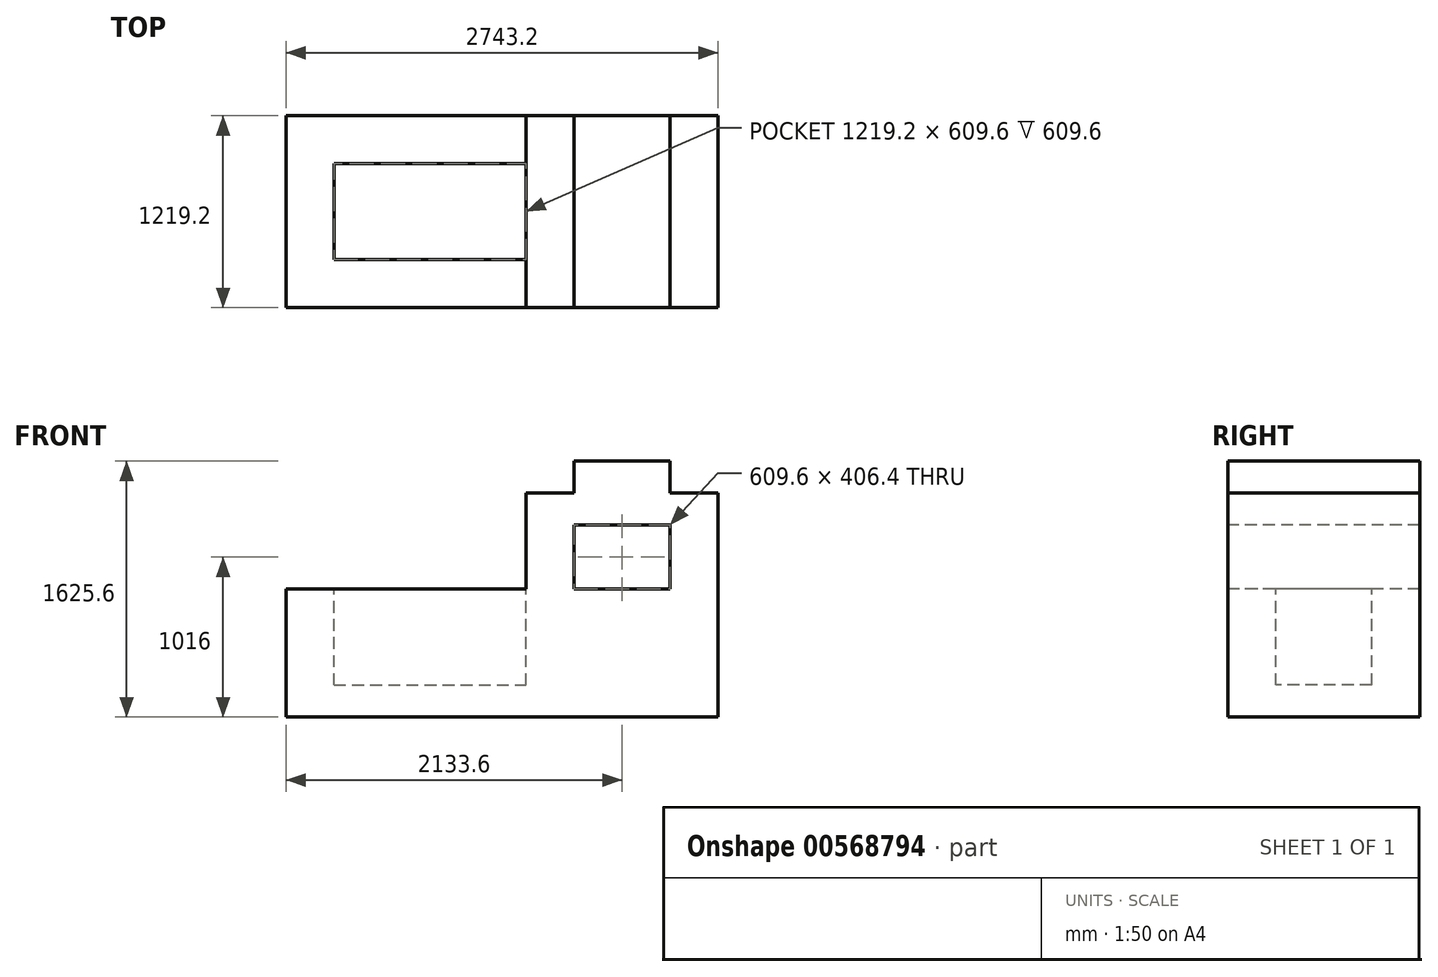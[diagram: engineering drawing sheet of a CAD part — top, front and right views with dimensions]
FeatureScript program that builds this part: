
annotation { "Feature Type Name" : "Feature", "Feature Type Description" : "" }
export const myFeature = defineFeature(function(context is Context, id is Id, definition is map)
    precondition{}
    {
        {
            var Q0;
            Q0=qCreatedBy(makeId("Front.planeOp"),FACE);
            var sketch = newSketch(context, id + "F0", { "sketchPlane" : qUnion([Q0])});
            skLineSegment(sketch, "E0.bottom", {"start": v(0, 0) * mm, "end": v(2743.2, 0) * mm});
            skLineSegment(sketch, "E0.top", {"start": v(0, 1625.6) * mm, "end": v(2743.2, 1625.6) * mm});
            skLineSegment(sketch, "E0.left", {"start": v(0, 0) * mm, "end": v(0, 1625.6) * mm});
            skLineSegment(sketch, "E0.right", {"start": v(2743.2, 0) * mm, "end": v(2743.2, 1625.6) * mm});
            skSolve(sketch);
        }
        {
            var Q0;
            Q0=makeQuery(id+"F0.imprint","IMPRINT",FACE,{"disambiguationData":[TD([[makeQuery(id+"F0.imprint","IMPRINT",EDGE,{"derivedFrom":sQuery(id+"F0.wireOp",EDGE,"E0.bottom")}),1.0]])]});
            extrude(context, id + "F1", {"entities" : qUnion([Q0]), "depth" : 1219.2 * mm, "offsetDistance" : 25.4 * mm});
        }
        {
            var Q0;
            Q0=makeQuery(id+"F1.opExtrude","CAP_FACE",FACE,{"disambiguationData":[OSD([sQuery(id+"F0.wireOp",EDGE,"E0.bottom"),sQuery(id+"F0.wireOp",EDGE,"E0.top"),sQuery(id+"F0.wireOp",EDGE,"E0.left"),sQuery(id+"F0.wireOp",EDGE,"E0.right")])],"isStart":false});
            var sketch = newSketch(context, id + "F2", { "sketchPlane" : qUnion([Q0])});
            skLineSegment(sketch, "E1.bottom", {"start": v(2743.2, 1625.6) * mm, "end": v(2438.4, 1625.6) * mm});
            skLineSegment(sketch, "E1.top", {"start": v(2743.2, 1422.4) * mm, "end": v(2438.4, 1422.4) * mm});
            skLineSegment(sketch, "E1.left", {"start": v(2743.2, 1625.6) * mm, "end": v(2743.2, 1422.4) * mm});
            skLineSegment(sketch, "E1.right", {"start": v(2438.4, 1625.6) * mm, "end": v(2438.4, 1422.4) * mm});
            skSolve(sketch);
        }
        {
            var Q0;
            Q0=makeQuery(id+"F2.imprint","IMPRINT",FACE,{"disambiguationData":[TD([[makeQuery(id+"F2.imprint","IMPRINT",EDGE,{"derivedFrom":sQuery(id+"F2.wireOp",EDGE,"E1.bottom")}),-1.0]])]});
            extrude(context, id + "F3", {"entities" : qUnion([Q0]), "operationType" : NewBodyOperationType.REMOVE, "endBound" : BoundingType.THROUGH_ALL, "oppositeDirection" : true, "depth" : 25.4 * mm, "offsetDistance" : 25.4 * mm});
        }
        {
            var Q0;
            Q0=makeQuery(id+"F1.opExtrude","CAP_FACE",FACE,{"disambiguationData":[OSD([sQuery(id+"F0.wireOp",EDGE,"E0.bottom"),sQuery(id+"F0.wireOp",EDGE,"E0.top"),sQuery(id+"F0.wireOp",EDGE,"E0.left"),sQuery(id+"F0.wireOp",EDGE,"E0.right")])],"isStart":false});
            var sketch = newSketch(context, id + "F4", { "sketchPlane" : qUnion([Q0])});
            skLineSegment(sketch, "E2.bottom", {"start": v(0, 1625.6) * mm, "end": v(1524, 1625.6) * mm});
            skLineSegment(sketch, "E2.top", {"start": v(0, 812.8) * mm, "end": v(1524, 812.8) * mm});
            skLineSegment(sketch, "E2.left", {"start": v(0, 1625.6) * mm, "end": v(0, 812.8) * mm});
            skLineSegment(sketch, "E2.right", {"start": v(1524, 1625.6) * mm, "end": v(1524, 812.8) * mm});
            skSolve(sketch);
        }
        {
            var Q0;
            Q0=makeQuery(id+"F4.imprint","IMPRINT",FACE,{"disambiguationData":[TD([[makeQuery(id+"F4.imprint","IMPRINT",EDGE,{"derivedFrom":sQuery(id+"F4.wireOp",EDGE,"E2.bottom")}),-1.0]])]});
            extrude(context, id + "F5", {"entities" : qUnion([Q0]), "operationType" : NewBodyOperationType.REMOVE, "endBound" : BoundingType.THROUGH_ALL, "oppositeDirection" : true, "depth" : 25.4 * mm, "offsetDistance" : 25.4 * mm});
        }
        {
            var Q0;
            Q0=makeQuery(id+"F1.opExtrude","CAP_FACE",FACE,{"disambiguationData":[OSD([sQuery(id+"F0.wireOp",EDGE,"E0.bottom"),sQuery(id+"F0.wireOp",EDGE,"E0.top"),sQuery(id+"F0.wireOp",EDGE,"E0.left"),sQuery(id+"F0.wireOp",EDGE,"E0.right")])],"isStart":false});
            var sketch = newSketch(context, id + "F6", { "sketchPlane" : qUnion([Q0])});
            skLineSegment(sketch, "E3.bottom", {"start": v(1524, 1625.6) * mm, "end": v(1828.8, 1625.6) * mm});
            skLineSegment(sketch, "E3.top", {"start": v(1524, 1422.4) * mm, "end": v(1828.8, 1422.4) * mm});
            skLineSegment(sketch, "E3.left", {"start": v(1524, 1625.6) * mm, "end": v(1524, 1422.4) * mm});
            skLineSegment(sketch, "E3.right", {"start": v(1828.8, 1625.6) * mm, "end": v(1828.8, 1422.4) * mm});
            skSolve(sketch);
        }
        {
            var Q0;
            Q0=makeQuery(id+"F6.imprint","IMPRINT",FACE,{"disambiguationData":[TD([[makeQuery(id+"F6.imprint","IMPRINT",EDGE,{"derivedFrom":sQuery(id+"F6.wireOp",EDGE,"E3.bottom")}),-1.0]])]});
            extrude(context, id + "F7", {"entities" : qUnion([Q0]), "operationType" : NewBodyOperationType.REMOVE, "endBound" : BoundingType.THROUGH_ALL, "oppositeDirection" : true, "depth" : 25.4 * mm, "offsetDistance" : 25.4 * mm});
        }
        {
            var Q0;
            Q0=makeQuery(id+"F1.opExtrude","CAP_FACE",FACE,{"disambiguationData":[OSD([sQuery(id+"F0.wireOp",EDGE,"E0.bottom"),sQuery(id+"F0.wireOp",EDGE,"E0.top"),sQuery(id+"F0.wireOp",EDGE,"E0.left"),sQuery(id+"F0.wireOp",EDGE,"E0.right")])],"isStart":false});
            var sketch = newSketch(context, id + "F8", { "sketchPlane" : qUnion([Q0])});
            skLineSegment(sketch, "E4.bottom", {"start": v(1828.8, 1219.2) * mm, "end": v(2438.4, 1219.2) * mm});
            skLineSegment(sketch, "E4.top", {"start": v(1828.8, 812.8) * mm, "end": v(2438.4, 812.8) * mm});
            skLineSegment(sketch, "E4.left", {"start": v(1828.8, 1219.2) * mm, "end": v(1828.8, 812.8) * mm});
            skLineSegment(sketch, "E4.right", {"start": v(2438.4, 1219.2) * mm, "end": v(2438.4, 812.8) * mm});
            skSolve(sketch);
        }
        {
            var Q0;
            Q0=makeQuery(id+"F8.imprint","IMPRINT",FACE,{"disambiguationData":[TD([[makeQuery(id+"F8.imprint","IMPRINT",EDGE,{"derivedFrom":sQuery(id+"F8.wireOp",EDGE,"E4.bottom")}),-1.0]])]});
            extrude(context, id + "F9", {"entities" : qUnion([Q0]), "operationType" : NewBodyOperationType.REMOVE, "endBound" : BoundingType.THROUGH_ALL, "oppositeDirection" : true, "depth" : 25.4 * mm, "offsetDistance" : 25.4 * mm});
        }
        {
            var Q0;
            Q0=makeQuery(id+"F5.boolean.opBoolean","COPY",FACE,{"derivedFrom":makeQuery(id+"F5.opExtrude","SWEPT_FACE",FACE,{"disambiguationData":[OSD([sQuery(id+"F4.wireOp",EDGE,"E2.top")])]})});
            var sketch = newSketch(context, id + "F10", { "sketchPlane" : qUnion([Q0])});
            skLineSegment(sketch, "E5.bottom", {"start": v(304.8, -304.8) * mm, "end": v(1524, -304.8) * mm});
            skLineSegment(sketch, "E5.top", {"start": v(304.8, -914.4) * mm, "end": v(1524, -914.4) * mm});
            skLineSegment(sketch, "E5.left", {"start": v(304.8, -304.8) * mm, "end": v(304.8, -914.4) * mm});
            skLineSegment(sketch, "E5.right", {"start": v(1524, -304.8) * mm, "end": v(1524, -914.4) * mm});
            skSolve(sketch);
        }
        {
            var Q0;
            Q0=makeQuery(id+"F10.imprint","IMPRINT",FACE,{"disambiguationData":[TD([[makeQuery(id+"F10.imprint","IMPRINT",EDGE,{"derivedFrom":sQuery(id+"F10.wireOp",EDGE,"E5.bottom")}),-1.0]])]});
            extrude(context, id + "F11", {"entities" : qUnion([Q0]), "operationType" : NewBodyOperationType.REMOVE, "oppositeDirection" : true, "depth" : 609.6 * mm, "offsetDistance" : 25.4 * mm});
        }
    });
